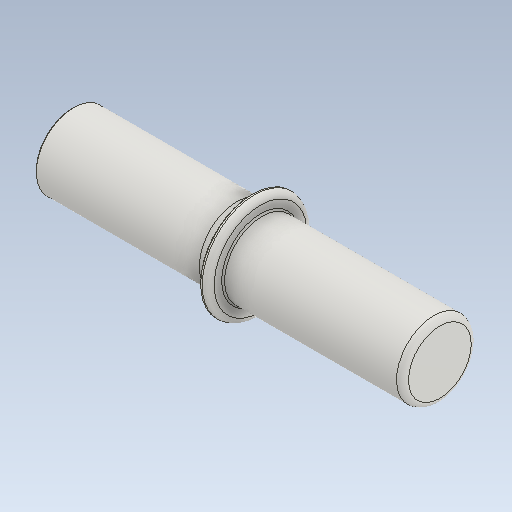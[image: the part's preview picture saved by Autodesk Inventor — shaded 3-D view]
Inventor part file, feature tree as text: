
AUTODESK INVENTOR PART (.ipt)
format: ipt  version: 2021 (Build 250183000, 183)  size: 152,576 bytes
history: native  units: mm
features: chamfer x3, fillet x3, other x3, revolve x1
ambient origin geometry x6: Origin, XZ Plane, XY Plane, X Axis, Y Axis, Z Axis
bodies: Solid1 (feature_tree)
feature tree (10):
  revolve  "Revolution1"  [1 undecoded]
  chamfer  "Chamfer3"  Distance=25.0mm
  fillet  "Fillet2"  Radius=35.0mm
  chamfer  "Chamfer4"  Distance=25.0mm
  fillet  "Fillet3"  [1 undecoded]
  chamfer  "Chamfer1"  Distance=0.5mm Angle=45.0deg
  fillet  "Fillet1"  Radius=5.0mm
  other  "Start Plane"
  other  "Origin point"
  other  "Main Sketch"
note: 2 required parameter values undecoded (feature->parameter linkage not recoverable at this tier; creation-order binding heuristic only, values carry confidence <= 0.55)